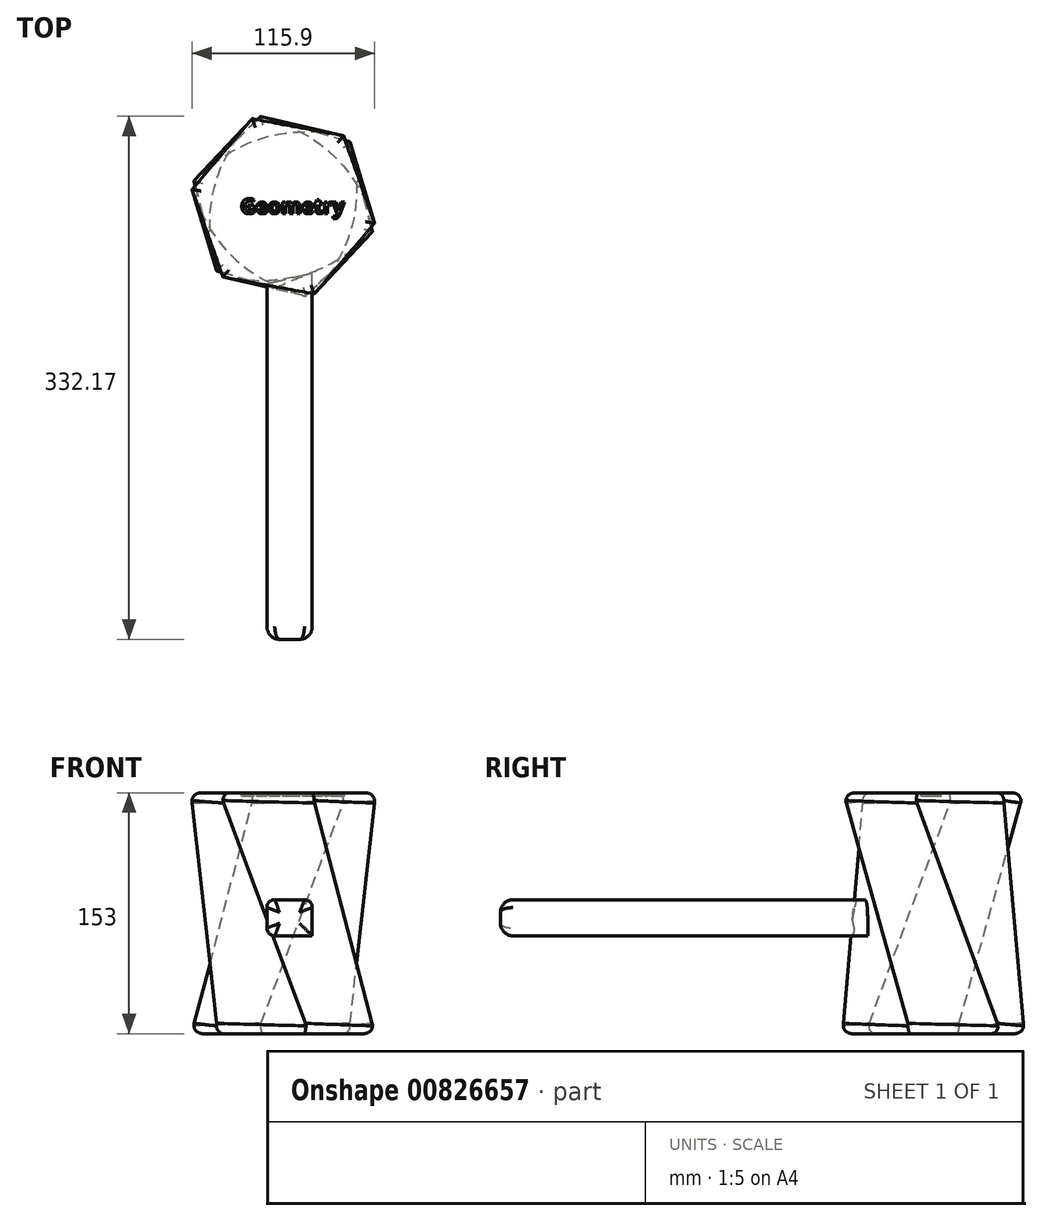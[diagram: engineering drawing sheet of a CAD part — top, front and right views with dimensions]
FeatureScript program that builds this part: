
annotation { "Feature Type Name" : "Feature", "Feature Type Description" : "" }
export const myFeature = defineFeature(function(context is Context, id is Id, definition is map)
    precondition{}
    {
        {
            var Q0;
            Q0=qCreatedBy(makeId("Top.planeOp"),FACE);
            cPlane(context, id + "F0", {"entities" : qUnion([Q0]), "cplaneType" : CPlaneType.OFFSET, "offset" : 153 * mm, "width" : 150 * mm, "height" : 150 * mm});
        }
        {
            var Q0;
            Q0=qCreatedBy(id+"F0.planeOp",FACE);
            var sketch = newSketch(context, id + "F1", { "sketchPlane" : qUnion([Q0])});
            skCircle(sketch, "E0.cCircle", {"center": v(0, 0) * mm, "radius": 51.96 * mm, "construction": true});
            skLineSegment(sketch, "E0.0", {"start": v(58.6, -12.9) * mm, "end": v(18.13, -57.2) * mm});
            skLineSegment(sketch, "E0.1", {"start": v(18.13, -57.2) * mm, "end": v(-40.46, -44.3) * mm});
            skLineSegment(sketch, "E0.2", {"start": v(-40.46, -44.3) * mm, "end": v(-58.6, 12.9) * mm});
            skLineSegment(sketch, "E0.3", {"start": v(-58.6, 12.9) * mm, "end": v(-18.13, 57.2) * mm});
            skLineSegment(sketch, "E0.4", {"start": v(-18.13, 57.2) * mm, "end": v(40.46, 44.3) * mm});
            skLineSegment(sketch, "E0.5", {"start": v(40.46, 44.3) * mm, "end": v(58.6, -12.9) * mm});
            skPoint(sketch, "E0.0.midPoint", {"position": v(38.37, -35.04) * mm});
            skSolve(sketch);
        }
        {
            var Q0;
            Q0=qCreatedBy(makeId("Top.planeOp"),FACE);
            var sketch = newSketch(context, id + "F2", { "sketchPlane" : qUnion([Q0])});
            skCircle(sketch, "E1.cCircle", {"center": v(0, 0) * mm, "radius": 51.96 * mm, "construction": true});
            skLineSegment(sketch, "E1.0", {"start": v(16.52, -57.68) * mm, "end": v(-41.7, -43.14) * mm});
            skLineSegment(sketch, "E1.1", {"start": v(-41.7, -43.14) * mm, "end": v(-58.21, 14.54) * mm});
            skLineSegment(sketch, "E1.2", {"start": v(-58.21, 14.54) * mm, "end": v(-16.52, 57.68) * mm});
            skLineSegment(sketch, "E1.3", {"start": v(-16.52, 57.68) * mm, "end": v(41.7, 43.14) * mm});
            skLineSegment(sketch, "E1.4", {"start": v(41.7, 43.14) * mm, "end": v(58.21, -14.54) * mm});
            skLineSegment(sketch, "E1.5", {"start": v(58.21, -14.54) * mm, "end": v(16.52, -57.68) * mm});
            skPoint(sketch, "E1.0.midPoint", {"position": v(-12.59, -50.41) * mm});
            skSolve(sketch);
        }
        {
            var Q0;
            Q0=makeQuery(id+"F2.imprint","IMPRINT",FACE,{"disambiguationData":[TD([[makeQuery(id+"F2.imprint","IMPRINT",EDGE,{"derivedFrom":sQuery(id+"F2.wireOp",EDGE,"E1.0")}),-1.0]])]});
            var Q1;
            Q1=makeQuery(id+"F1.imprint","IMPRINT",FACE,{"disambiguationData":[TD([[makeQuery(id+"F1.imprint","IMPRINT",EDGE,{"derivedFrom":sQuery(id+"F1.wireOp",EDGE,"E0.0")}),-1.0]])]});
            var Q2;
            Q2=sQuery(id+"F2.wireOp",VERTEX,"E1.3.end");
            var Q3;
            Q3=sQuery(id+"F1.wireOp",VERTEX,"E0.0.start");
            loft(context, id + "F3", {"sheetProfilesArray" : [{ "sheetProfileEntities" : qUnion([Q0]) }, { "sheetProfileEntities" : qUnion([Q1]) }], "matchConnections" : true, "connections" : [{ "connectionEntities" : qUnion([Q2, Q3]), "connectionEdgeQueries" : qUnion([]), "connectionEdgeParameters" : [] }]});
        }
        {
            var Q0;
            Q0=makeQuery(id+"F3.opLoft","MID_CAP_EDGE",EDGE,{"disambiguationData":[OSD([sQuery(id+"F1.wireOp",EDGE,"E0.1"),sQuery(id+"F1.wireOp",EDGE,"E0.2"),sQuery(id+"F1.wireOp",EDGE,"E0.3")])],"capPos":1.0});
            var Q1;
            Q1=makeQuery(id+"F3.opLoft","MID_CAP_EDGE",EDGE,{"disambiguationData":[OSD([sQuery(id+"F1.wireOp",EDGE,"E0.0"),sQuery(id+"F1.wireOp",EDGE,"E0.1"),sQuery(id+"F1.wireOp",EDGE,"E0.2")])],"capPos":1.0});
            var Q2;
            Q2=makeQuery(id+"F3.opLoft","MID_CAP_EDGE",EDGE,{"disambiguationData":[OSD([sQuery(id+"F1.wireOp",EDGE,"E0.2"),sQuery(id+"F1.wireOp",EDGE,"E0.3"),sQuery(id+"F1.wireOp",EDGE,"E0.4")])],"capPos":1.0});
            var Q3;
            Q3=makeQuery(id+"F3.opLoft","MID_CAP_EDGE",EDGE,{"disambiguationData":[OSD([sQuery(id+"F1.wireOp",EDGE,"E0.3"),sQuery(id+"F1.wireOp",EDGE,"E0.4"),sQuery(id+"F1.wireOp",EDGE,"E0.5")])],"capPos":1.0});
            var Q4;
            Q4=makeQuery(id+"F3.opLoft","MID_CAP_EDGE",EDGE,{"disambiguationData":[OSD([sQuery(id+"F1.wireOp",EDGE,"E0.0"),sQuery(id+"F1.wireOp",EDGE,"E0.4"),sQuery(id+"F1.wireOp",EDGE,"E0.5")])],"capPos":1.0});
            var Q5;
            Q5=makeQuery(id+"F3.opLoft","MID_CAP_EDGE",EDGE,{"disambiguationData":[OSD([sQuery(id+"F1.wireOp",EDGE,"E0.0"),sQuery(id+"F1.wireOp",EDGE,"E0.1"),sQuery(id+"F1.wireOp",EDGE,"E0.5")])],"capPos":1.0});
            var Q6;
            Q6=makeQuery(id+"F3.opLoft","MID_CAP_EDGE",EDGE,{"disambiguationData":[OSD([sQuery(id+"F2.wireOp",EDGE,"E1.0"),sQuery(id+"F2.wireOp",EDGE,"E1.1"),sQuery(id+"F2.wireOp",EDGE,"E1.5")])],"capPos":0.0});
            var Q7;
            Q7=makeQuery(id+"F3.opLoft","MID_CAP_EDGE",EDGE,{"disambiguationData":[OSD([sQuery(id+"F2.wireOp",EDGE,"E1.0"),sQuery(id+"F2.wireOp",EDGE,"E1.1"),sQuery(id+"F2.wireOp",EDGE,"E1.2")])],"capPos":0.0});
            var Q8;
            Q8=makeQuery(id+"F3.opLoft","MID_CAP_EDGE",EDGE,{"disambiguationData":[OSD([sQuery(id+"F2.wireOp",EDGE,"E1.1"),sQuery(id+"F2.wireOp",EDGE,"E1.2"),sQuery(id+"F2.wireOp",EDGE,"E1.3")])],"capPos":0.0});
            var Q9;
            Q9=makeQuery(id+"F3.opLoft","MID_CAP_EDGE",EDGE,{"disambiguationData":[OSD([sQuery(id+"F2.wireOp",EDGE,"E1.2"),sQuery(id+"F2.wireOp",EDGE,"E1.3"),sQuery(id+"F2.wireOp",EDGE,"E1.4")])],"capPos":0.0});
            var Q10;
            Q10=makeQuery(id+"F3.opLoft","MID_CAP_EDGE",EDGE,{"disambiguationData":[OSD([sQuery(id+"F2.wireOp",EDGE,"E1.3"),sQuery(id+"F2.wireOp",EDGE,"E1.4"),sQuery(id+"F2.wireOp",EDGE,"E1.5")])],"capPos":0.0});
            var Q11;
            Q11=makeQuery(id+"F3.opLoft","MID_CAP_EDGE",EDGE,{"disambiguationData":[OSD([sQuery(id+"F2.wireOp",EDGE,"E1.0"),sQuery(id+"F2.wireOp",EDGE,"E1.4"),sQuery(id+"F2.wireOp",EDGE,"E1.5")])],"capPos":0.0});
            fillet(context, id + "F4", {"entities" : qUnion([Q0, Q1, Q2, Q3, Q4, Q5, Q6, Q7, Q8, Q9, Q10, Q11]), "radius" : 5 * mm, "tangentPropagation" : true, "allowEdgeOverflow" : false});
        }
        {
            var Q0;
            Q0=qCreatedBy(makeId("Front.planeOp"),FACE);
            cPlane(context, id + "F5", {"entities" : qUnion([Q0]), "cplaneType" : CPlaneType.OFFSET, "offset" : 20 * mm, "width" : 150 * mm, "height" : 150 * mm});
        }
        {
            var Q0;
            Q0=qCreatedBy(id+"F5.planeOp",FACE);
            var sketch = newSketch(context, id + "F6", { "sketchPlane" : qUnion([Q0])});
            skLineSegment(sketch, "E2.bottom", {"start": v(18.43, 85.1) * mm, "end": v(-10.36, 85.1) * mm});
            skLineSegment(sketch, "E2.top", {"start": v(18.43, 62.1) * mm, "end": v(-10.36, 62.1) * mm});
            skLineSegment(sketch, "E2.left", {"start": v(18.43, 85.1) * mm, "end": v(18.43, 62.1) * mm});
            skLineSegment(sketch, "E2.right", {"start": v(-10.36, 85.1) * mm, "end": v(-10.36, 62.1) * mm});
            skSolve(sketch);
        }
        {
            var Q0;
            Q0 = qSketchRegion(id + "F6", true);
            extrude(context, id + "F7", {"entities" : qUnion([Q0]), "operationType" : NewBodyOperationType.ADD, "depth" : 255 * mm, "offsetDistance" : 25 * mm});
        }
        {
            var Q0;
            Q0=makeQuery(id+"F7.opExtrude","SWEPT_EDGE",EDGE,{"disambiguationData":[OSD([sQuery(id+"F6.wireOp",EDGE,"E2.bottom"),sQuery(id+"F6.wireOp",EDGE,"E2.left")])]});
            var Q1;
            Q1=makeQuery(id+"F7.opExtrude","SWEPT_EDGE",EDGE,{"disambiguationData":[OSD([sQuery(id+"F6.wireOp",EDGE,"E2.bottom"),sQuery(id+"F6.wireOp",EDGE,"E2.right")])]});
            var Q2;
            Q2=makeQuery(id+"F7.opExtrude","SWEPT_EDGE",EDGE,{"disambiguationData":[OSD([sQuery(id+"F6.wireOp",EDGE,"E2.top"),sQuery(id+"F6.wireOp",EDGE,"E2.right")])]});
            fillet(context, id + "F8", {"entities" : qUnion([Q0, Q1, Q2]), "radius" : 5 * mm, "tangentPropagation" : true, "allowEdgeOverflow" : false});
        }
        {
            var Q0;
            Q0=makeQuery(id+"F7.opExtrude","CAP_FACE",FACE,{"disambiguationData":[OSD([sQuery(id+"F6.wireOp",EDGE,"E2.bottom"),sQuery(id+"F6.wireOp",EDGE,"E2.top"),sQuery(id+"F6.wireOp",EDGE,"E2.left"),sQuery(id+"F6.wireOp",EDGE,"E2.right")])],"isStart":false});
            fillet(context, id + "F9", {"entities" : qUnion([Q0]), "radius" : 8 * mm, "tangentPropagation" : true, "allowEdgeOverflow" : false});
        }
        {
            var Q0;
            Q0=makeQuery(id+"F3.opLoft","CAP_FACE",FACE,{"disambiguationData":[OSD([makeQuery(id+"F1.imprint","IMPRINT",FACE,{"disambiguationData":[TD([[makeQuery(id+"F1.imprint","IMPRINT",EDGE,{"derivedFrom":sQuery(id+"F1.wireOp",EDGE,"E0.0")}),-1.0]])]})])],"isStart":true});
            var sketch = newSketch(context, id + "F10", { "sketchPlane" : qUnion([Q0])});
            skText(sketch, "E3", { "text": "Geometry", "fontName": "OpenSans-Bold.ttf"});
            const initialGuessF10  = {"E3": [-0.02714, -0.00463, 1, 0, 0.00957]};
            skSetInitialGuess(sketch, initialGuessF10);
            skSolve(sketch);
        }
        {
            var Q0;
            Q0 = qSketchRegion(id + "F10", true);
            extrude(context, id + "F11", {"entities" : qUnion([Q0]), "operationType" : NewBodyOperationType.REMOVE, "oppositeDirection" : true, "depth" : 2 * mm, "offsetDistance" : 25 * mm});
        }
    });
